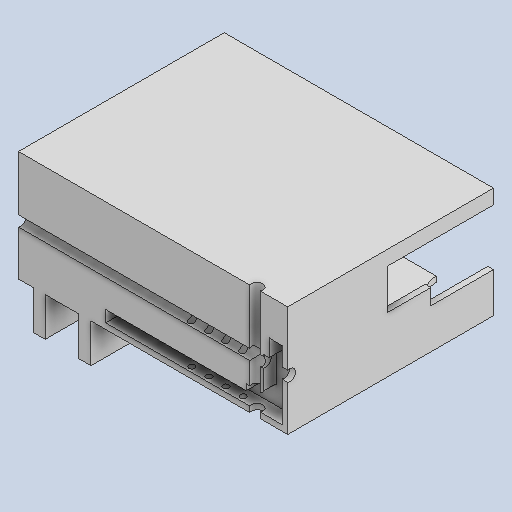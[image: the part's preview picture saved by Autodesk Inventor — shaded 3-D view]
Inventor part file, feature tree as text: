
AUTODESK INVENTOR PART (.ipt)
format: ipt  version: 2022 (Build 260153000, 153)  size: 367,616 bytes
history: native  units: in
note: dims shown in document units (in); Inventor stores cm internally (conversion verified against a paired STEP export)
features: reference x21, sketch x13, other x11, extrude x11, projected_geometry x3, plane x2, fillet x1
ambient origin geometry x8: Origin, YZ Plane, XZ Plane, XY Plane, X Axis, Y Axis, Z Axis, Center Point
bodies: Solid1 (feature_tree)
feature tree (62):
  other  "Lower Support.ipt"
  extrude  "Extrusion1"  Depth=0.3937in TaperAngle=0.0deg
  extrude  "Extrusion2"  TaperAngle=0.0deg  [1 undecoded]
  extrude  "Extrusion3"  Depth=0.0039in
  plane  "Work Plane2"
  extrude  "Extrusion4"  Depth=0.1969in
  extrude  "Extrusion7"  Depth=0.7874in
  extrude  "Extrusion8"  Depth=0.3937in
  extrude  "Extrusion12"  Depth=0.1969in
  fillet  "Fillet4"  Radius=0.1969in
  sketch  "Sketch22"  dims[d69=0.1969in d70=0.1969in]
  plane  "Work Plane3"
  extrude  "Extrusion16"  Depth=0.3937in TaperAngle=0.0deg
  extrude  "Extrusion17"  TaperAngle=0.0deg  [1 undecoded]
  extrude  "Extrusion18"  Depth=0.1969in
  extrude  "Extrusion19"  Depth=0.1969in
  other  "Solid1::Lower Support.ipt"
  other  "TaggingFeature1"
  sketch  "Sketch1"  dims[d0=0.3937in d1=0.3937in d2=0.0in]
  sketch  "Sketch4"  dims[d3=0.0in d4=0.0in d5=0.0in d6=0.0in]
  sketch  "Sketch5"  dims[d7=7.4803in d8=0.0in d14=0.0039in]
  sketch  "Sketch6"  dims[d15=0.1969in d16=0.0in d17=0.1969in]
  projected_geometry  "Projected Loop1"
  sketch  "Sketch7"  dims[d18=6.2992in d19=0.0in d39=0.7874in]
  sketch  "Sketch8"  dims[d41=0.3937in d42=0.0in d43=0.3937in]
  sketch  "Sketch9"  dims[d44=0.1969in d61=0.0039in d62=0.1969in]
  projected_geometry  "Projected Loop2"
  sketch  "Sketch13"  dims[d63=0.0039in d64=0.3937in d65=0.0in]
  reference  "Reference2"
  sketch  "Sketch14"  dims[d66=0.2323in d67=0.0in d68=0.0in]
  projected_geometry  "Projected Loop3"
  reference  "Reference25"
  reference  "Reference26"
  reference  "Reference27"
  reference  "Reference28"
  reference  "Reference29"
  sketch  "Sketch23"  dims[d71=0.1969in d72=0.1969in]
  reference  "Reference30"
  reference  "Reference31"
  sketch  "Sketch24"  dims[d73=0.1969in]
  reference  "Reference32"
  reference  "Reference33"
  reference  "Reference34"
  reference  "Reference35"
  reference  "Reference36"
  reference  "Reference37"
  reference  "Reference38"
  reference  "Reference39"
  reference  "Reference40"
  reference  "Reference41"
  reference  "Reference42"
  reference  "Reference43"
  sketch  "Sketch25"  dims[d74=0.1969in d75=0.1969in d76=0.1969in d77=0.1969in d78=0.0in d79=0.0in d80=0.0in d81=0.0in]
  reference  "Reference44"
  other  "Linear Rail Assembly.iam"
  other  "backboard_MIR:1"
  other  "linear actuator:1"
  other  "Power brick assembly:1"
  other  "IEC 320 C13 Cable End:1"
  other  "printer power brick assembly:2"
  other  "printer power brick assembly:1"
  other  "Lower Support:1"
note: 2 required parameter values undecoded (feature->parameter linkage not recoverable at this tier; creation-order binding heuristic only, values carry confidence <= 0.55)
